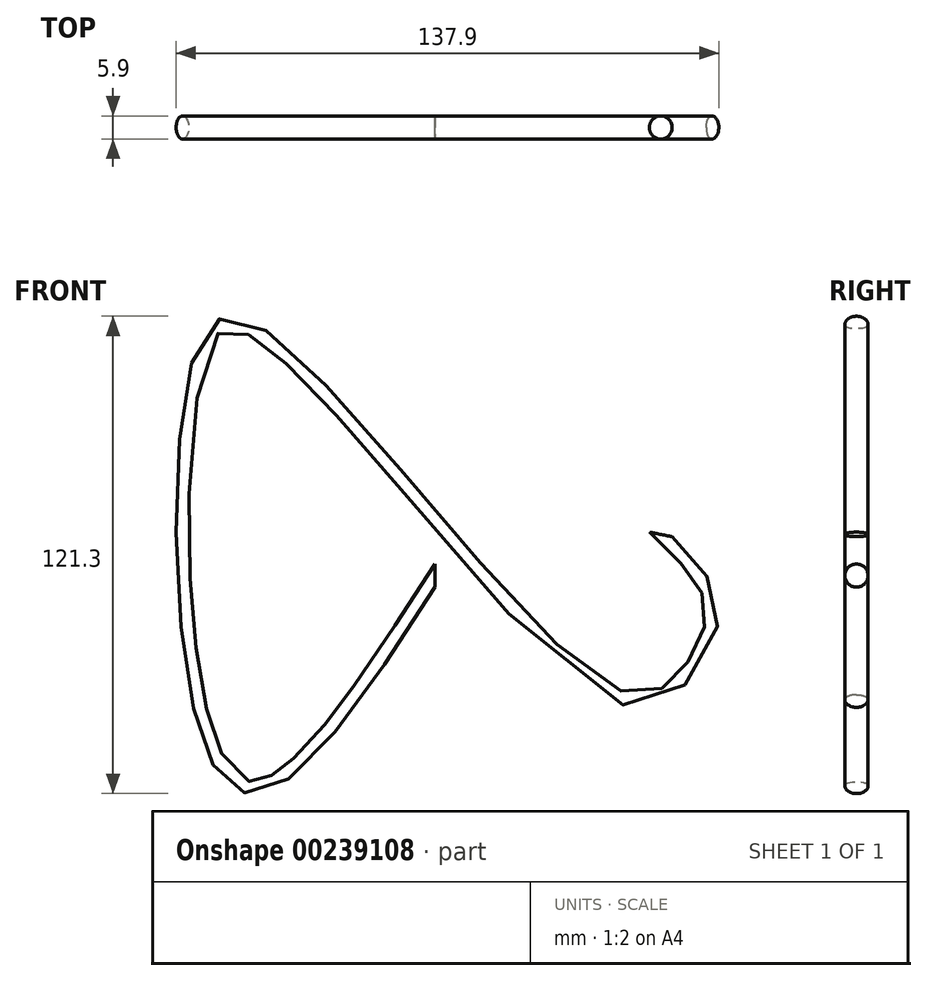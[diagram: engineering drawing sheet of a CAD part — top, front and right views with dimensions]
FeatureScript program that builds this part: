
annotation { "Feature Type Name" : "Feature", "Feature Type Description" : "" }
export const myFeature = defineFeature(function(context is Context, id is Id, definition is map)
    precondition{}
    {
        {
            var Q0;
            Q0=qCreatedBy(makeId("Front.planeOp"),FACE);
            var sketch = newSketch(context, id + "F0", { "sketchPlane" : qUnion([Q0])});
            skFitSpline(sketch, "E0", {"points": [v(0, 0) * mm, v(-43.38, -53.05) * mm, v(-56.93, -42.99) * mm, v(-61.58, 48.02) * mm, v(-48.02, 63.12) * mm, v(42.98, -29.04) * mm, v(63.5, -25.17) * mm, v(70.09, -7.36) * mm, v(57.31, 10.46) * mm], "startDerivative": vector(-297.94, -460.8) * mm, "endDerivative": vector(-192.84, 187.45) * mm});
            skSolve(sketch);
        }
        {
            var Q0;
            Q0=qCreatedBy(makeId("Right.planeOp"),FACE);
            var sketch = newSketch(context, id + "F1", { "sketchPlane" : qUnion([Q0])});
            skCircle(sketch, "E1", {"center": v(0, 0) * mm, "radius": 2.95 * mm});
            skSolve(sketch);
        }
        {
            var Q0;
            Q0=makeQuery(id+"F1.imprint","IMPRINT",FACE,{"disambiguationData":[TD([[makeQuery(id+"F1.imprint","IMPRINT",EDGE,{"derivedFrom":sQuery(id+"F1.wireOp",EDGE,"E1")}),1.0]])]});
            var Q1;
            Q1=sQuery(id+"F0.wireOp",EDGE,"E0");
            sweep(context, id + "F2", {"profiles" : qUnion([Q0]), "path" : qUnion([Q1])});
        }
    });
